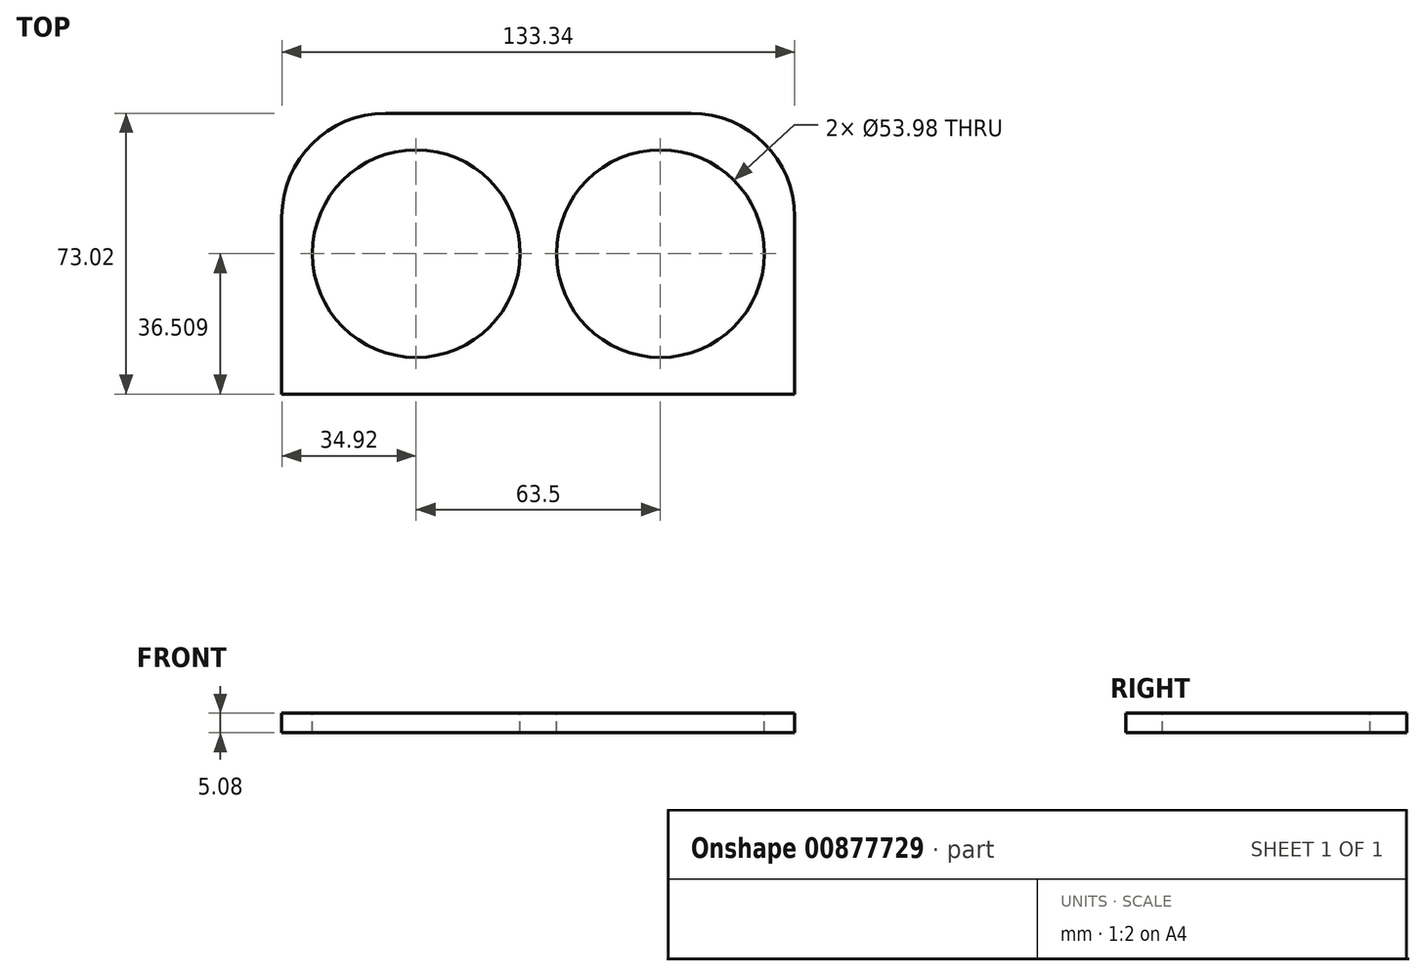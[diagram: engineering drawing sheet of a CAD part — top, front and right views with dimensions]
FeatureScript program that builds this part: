
annotation { "Feature Type Name" : "Feature", "Feature Type Description" : "" }
export const myFeature = defineFeature(function(context is Context, id is Id, definition is map)
    precondition{}
    {
        {
            var Q0;
            Q0=qCreatedBy(makeId("Front.planeOp"),FACE);
            var sketch = newSketch(context, id + "F0", { "sketchPlane" : qUnion([Q0])});
            skCircle(sketch, "E0", {"center": v(31.75, 0) * mm, "radius": 26.99 * mm});
            skCircle(sketch, "E1.1.0.0", {"center": v(-31.75, 0) * mm, "radius": 26.99 * mm});
            skLineSegment(sketch, "E1.direction1", {"start": v(31.75, 0) * mm, "end": v(-31.75, 0) * mm, "construction": true});
            skLineSegment(sketch, "E2.bottom", {"start": v(-66.67, 36.51) * mm, "end": v(66.68, 36.51) * mm});
            skLineSegment(sketch, "E2.top", {"start": v(-39.72, -36.51) * mm, "end": v(39.69, -36.51) * mm});
            skLineSegment(sketch, "E2.left", {"start": v(-66.67, 36.51) * mm, "end": v(-66.68, -9.56) * mm});
            skLineSegment(sketch, "E2.right", {"start": v(66.68, 36.51) * mm, "end": v(66.68, -9.53) * mm});
            skPoint(sketch, "E2.middle", {"position": v(0, 0) * mm});
            skPoint(sketch, "E3.visualSharp", {"position": v(-66.68, -36.51) * mm});
            skArc(sketch, "E3.filletArc", {"start": v(-66.68, -9.56) * mm, "mid": v(-58.78, -28.62) * mm, "end": v(-39.72, -36.51) * mm});
            skPoint(sketch, "E4.visualSharp", {"position": v(66.68, -36.51) * mm});
            skArc(sketch, "E4.filletArc", {"start": v(39.69, -36.51) * mm, "mid": v(58.77, -28.6) * mm, "end": v(66.68, -9.53) * mm});
            skSolve(sketch);
        }
        {
            var Q0;
            Q0=makeQuery(id+"F0.imprint","IMPRINT",FACE,{"disambiguationData":[TD([[makeQuery(id+"F0.imprint","IMPRINT",EDGE,{"derivedFrom":sQuery(id+"F0.wireOp",EDGE,"E0")}),-1.0]])]});
            extrude(context, id + "F1", {"entities" : qUnion([Q0]), "depth" : 5.08 * mm, "offsetDistance" : 25.4 * mm});
        }
        {
            var Q0;
            Q0=makeQuery(id+"F1.opExtrude","SWEPT_BODY",BODY,{"disambiguationData":[OSD([sQuery(id+"F0.wireOp",EDGE,"E0"),sQuery(id+"F0.wireOp",EDGE,"E1.1.0.0"),sQuery(id+"F0.wireOp",EDGE,"E2.bottom"),sQuery(id+"F0.wireOp",EDGE,"E2.top"),sQuery(id+"F0.wireOp",EDGE,"E2.left"),sQuery(id+"F0.wireOp",EDGE,"E2.right"),sQuery(id+"F0.wireOp",EDGE,"E3.filletArc"),sQuery(id+"F0.wireOp",EDGE,"E4.filletArc")])]});
            var Q1;
            Q1=makeQuery(id+"F1.opExtrude","CAP_EDGE",EDGE,{"disambiguationData":[OSD([sQuery(id+"F0.wireOp",EDGE,"E2.bottom")])],"isStart":true});
            transform(context, id + "F2", {"entities" : qUnion([Q0]), "transformType" : TransformType.ROTATION, "transformAxis" : qUnion([Q1]), "angle" : 90 * degree, "makeCopy" : false});
        }
        {
            var Q0;
            Q0=makeQuery(id+"F1.opExtrude","SWEPT_BODY",BODY,{"disambiguationData":[OSD([sQuery(id+"F0.wireOp",EDGE,"E0"),sQuery(id+"F0.wireOp",EDGE,"E1.1.0.0"),sQuery(id+"F0.wireOp",EDGE,"E2.bottom"),sQuery(id+"F0.wireOp",EDGE,"E2.top"),sQuery(id+"F0.wireOp",EDGE,"E2.left"),sQuery(id+"F0.wireOp",EDGE,"E2.right"),sQuery(id+"F0.wireOp",EDGE,"E3.filletArc"),sQuery(id+"F0.wireOp",EDGE,"E4.filletArc")])]});
            transform(context, id + "F3", {"entities" : qUnion([Q0]), "transformType" : TransformType.TRANSLATION_3D, "dx" : 0 * mm, "dy" : -35.81 * mm, "dz" : -31.5 * mm, "makeCopy" : false});
        }
    });
